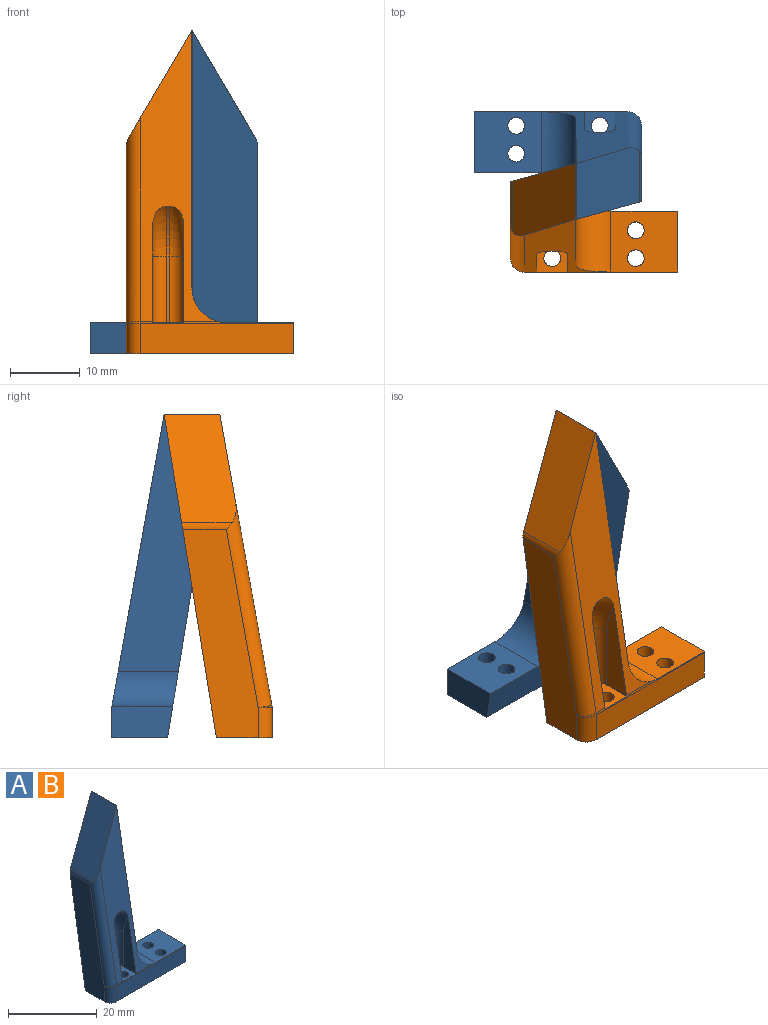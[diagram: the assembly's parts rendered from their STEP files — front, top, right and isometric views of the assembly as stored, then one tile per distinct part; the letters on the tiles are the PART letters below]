
ASSEMBLY  parts=2 mates=1
PART A: 27 faces, bbox 24x15.5x46.5 mm
  f0: plane 37x14.61mm, normal (1,0,0), area 307.8mm2, adj f1,f2,f4,f26
  f1: plane 41.83x11.09mm, normal (0,-0.98,0.18), area 200mm2, adj f0,f4,f5,f6,f10,f11,f12,f21
  f2: plane 46.51x24.01mm, normal (0,0.99,-0.16), area 438.5mm2, adj f0,f3,f4,f14,f16,f17,f25,f26
  f3: plane 29.96x10.83mm, normal (-1,0,0), area 193.4mm2, adj f2,f17,f22,f24,f25
  f4: plane 15.53x10.34mm, normal (-0.86,0,0.51), area 145.5mm2, adj f0,f1,f2,f24,f25
  f5: plane 14.18x3.99mm, normal (1,0,0), area 36.6mm2, adj f1,f9,f10,f13,f21
  f6: plane 14.18x3.99mm, normal (-1,0,0), area 36.6mm2, adj f1,f8,f12,f13,f21
  f7: plane 9.56x0.4mm, normal (0,-1,0), area 3.8mm2, adj f8,f9,f11,f13
  f8: cylinder r=2mm len=9.56mm, axis (0,0,-1), area 30mm2, adj f6,f7,f12,f13
  f9: cylinder r=2mm len=9.56mm, axis (0,0,1), area 30mm2, adj f5,f7,f10,f13
  f10: torus R=8mm, axis (-1,0,0), area 21.6mm2, adj f1,f5,f9,f11
  f11: cylinder r=10mm len=7.16mm, axis (-1,0,0), area 3.2mm2, adj f1,f7,f10,f12
  f12: torus R=8mm, axis (-1,0,0), area 21.6mm2, adj f1,f6,f8,f11
  f13: plane 5.99x4.4mm, normal (0,0,1), area 20.1mm2, adj f5,f6,f7,f8,f9,f20,f21
  f14: plane 9.6x8.72mm, normal (0,0,1), area 74.6mm2, adj f2,f16,f18,f19,f21,f26
  f15: plane 22x4.32mm, normal (0,-1,0), area 95.1mm2, adj f16,f17,f21,f22
  f16: plane 8.73x4.5mm, normal (1,0,0), area 37.6mm2, adj f2,f14,f15,f17,f21
  f17: plane 24x8mm, normal (0,0,-1), area 177.6mm2, adj f2,f3,f15,f16,f18,f19,f20,f22
  f18: cylinder r=1.2mm len=4.5mm, axis (0,0,-1), area 33.9mm2, adj f14,f17
  f19: cylinder r=1.2mm len=4.5mm, axis (0,0,-1), area 33.9mm2, adj f14,f17
  f20: cylinder r=1.2mm len=4.5mm, axis (0,0,-1), area 33.9mm2, adj f13,f17
  f21: cylinder r=2mm len=22mm, axis (1,0,0), area 5.2mm2, adj f1,f5,f6,f13,f14,f15,f16,f23
  f22: cylinder r=2mm len=4.32mm, axis (0,0,1), area 13.6mm2, adj f3,f15,f17,f23
  f23: sphere r=2mm, area 0.7mm2, adj f21,f22,f24
  f24: cylinder r=2mm len=29.58mm, axis (0,0.18,0.98), area 86.6mm2, adj f1,f3,f4,f23,f25
  f25: cylinder r=2mm len=7.27mm, axis (0,1,0), area 7.2mm2, adj f2,f3,f4,f24
  f26: cylinder r=5mm len=9.52mm, axis (0,-1,0), area 68.3mm2, adj f0,f1,f2,f14,f21
PART B: same geometry as A
PLACE A rot(axis=(0,0,1),180deg) t=(-17.99,22.87,10.25)mm
PLACE B t=(-12.81,7.87,10.25)mm fixed
MATE slider A.f16 <-> B.f16  axis (-1,0,0) through (-29.99,18.87,10.25)mm
